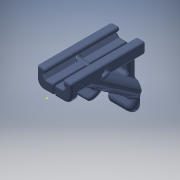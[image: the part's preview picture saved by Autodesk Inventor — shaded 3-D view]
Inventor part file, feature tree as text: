
AUTODESK INVENTOR PART (.ipt)
format: ipt  version: 2016 (Build 200138000, 138)  size: 5,970,432 bytes
history: native  units: mm
features: sketch x29, extrude x28, projected_geometry x27, fillet x26, plane x9, chamfer x3, other x2
ambient origin geometry x8: Origin, YZ Plane, XZ Plane, XY Plane, X Axis, Y Axis, Z Axis, Center Point
bodies: Solid1 (feature_tree)
feature tree (124):
  extrude  "Extrusion1"  Depth=35.0mm
  extrude  "Extrusion2"  Depth=10.0mm
  extrude  "Extrusion3"  Depth=12.0mm
  other  "Work Axis2"
  other  "Work Point2"
  plane  "Work Plane2"
  extrude  "Extrusion5"  Depth=12.0mm
  sketch  "Sketch9"  dims[d14=15.0mm d15=10.0mm d16=15.0mm d17=0.0mm]
  extrude  "Extrusion4"  TaperAngle=90.0deg  [1 undecoded]
  plane  "Work Plane3"
  sketch  "Sketch10"  dims[d18=17.0mm d19=10.0mm d20=130.0mm d21=0.0mm d23=35.531179mm d24=18.5mm d25=18.5mm d26=7.5mm]
  plane  "Work Plane5"
  extrude  "Extrusion8"  Depth=10.0mm
  fillet  "Fillet3"  Radius=15.0mm
  extrude  "Extrusion9"  Depth=10.0mm
  fillet  "Fillet5"  Radius=130.0mm
  fillet  "Fillet6"  Radius=35.531179mm
  fillet  "Fillet7"  Radius=18.5mm
  fillet  "Fillet8"  Radius=18.5mm
  fillet  "Fillet9"  Radius=7.5mm
  extrude  "Extrusion10"  Depth=36.0mm TaperAngle=0.0deg
  fillet  "Fillet10"  Radius=35.75mm
  fillet  "Fillet11"  [1 undecoded]
  fillet  "Fillet12"  Radius=34.0mm
  plane  "Work Plane4"
  extrude  "Extrusion11"  Depth=5.0mm
  extrude  "Extrusion12"  Depth=13.5mm TaperAngle=0.0deg
  extrude  "Extrusion13"  Depth=5.0mm
  fillet  "Fillet13"  Radius=2.0mm
  fillet  "Fillet14"  Radius=2.0mm
  fillet  "Fillet15"  Radius=2.0mm
  sketch  "Sketch22"  dims[d115=3.0mm d116=3.0mm d117=45.0deg]
  extrude  "Extrusion14"  Depth=9.0mm
  extrude  "Extrusion15"  Depth=8.5mm
  extrude  "Extrusion16"  Depth=3.0mm
  fillet  "Fillet16"  [1 undecoded]
  extrude  "Extrusion17"  Depth=2.0mm
  extrude  "Extrusion18"  Depth=1.0mm
  plane  "Work Plane6"
  extrude  "Extrusion19"  Depth=2.0mm
  sketch  "Sketch27"  dims[d132=5.0mm d133=2.0mm d134=8.0mm d135=8.0mm d136=5.0mm d137=0.0mm]
  extrude  "Extrusion21"  Depth=5.0mm
  extrude  "Extrusion22"  Depth=2.0mm
  fillet  "Fillet17"  Radius=8.0mm
  fillet  "Fillet18"  Radius=8.0mm
  fillet  "Fillet19"  Radius=5.0mm
  extrude  "Extrusion23"  Depth=5.0mm TaperAngle=0.0deg
  extrude  "Extrusion24"  Depth=0.5mm
  fillet  "Fillet20"  Radius=0.5mm
  chamfer  "Chamfer3"  Distance=55.0mm
  chamfer  "Chamfer4"  Distance=15.0mm
  fillet  "Fillet22"  Radius=1.0mm
  extrude  "Extrusion25"  Depth=5.0mm
  plane  "Work Plane7"
  extrude  "Extrusion26"  Depth=2.5mm
  fillet  "Fillet23"  Radius=1.0mm
  plane  "Work Plane8"
  plane  "Work Plane9"
  extrude  "Extrusion27"  Depth=1.0mm
  fillet  "Fillet25"  Radius=1.0mm
  fillet  "Fillet26"  Radius=1.0mm
  fillet  "Fillet28"  Radius=1.0mm
  fillet  "Fillet29"  Radius=1.0mm
  plane  "Work Plane10"
  extrude  "Extrusion28"  Depth=1.0mm
  extrude  "Extrusion29"  Depth=1.0mm
  extrude  "Extrusion30"  Depth=1.0mm
  fillet  "Fillet30"  Radius=1.0mm
  fillet  "Fillet31"  Radius=1.0mm
  fillet  "Fillet32"  Radius=1.0mm
  extrude  "Extrusion31"  Depth=1.0mm
  chamfer  "Chamfer5"  Distance=1.0mm
  sketch  "Sketch1"  dims[d0=135.0mm d1=35.0mm]
  sketch  "Sketch2"  dims[d2=10.0mm d3=0.0mm d4=10.0mm]
  projected_geometry  "Projected Loop1"
  sketch  "Sketch3"  dims[d5=15.0mm d6=0.0mm d7=12.0mm]
  projected_geometry  "Projected Loop2"
  sketch  "Sketch4"  dims[d10=9.599311mm d11=12.0mm]
  projected_geometry  "Projected Loop3"
  sketch  "Sketch5"  dims[d12=35.0mm d13=90.0deg]
  sketch  "Sketch12"  dims[d27=7.5mm d28=36.0mm d29=0.0mm d30=35.75mm d31=0.0mm d32=-5.0mm d44=34.0mm d45=0.0mm]
  projected_geometry  "Projected Loop11"
  sketch  "Sketch14"  dims[d46=5.0mm d48=5.0mm]
  sketch  "Sketch18"  dims[d49=5.0mm d50=13.5mm d51=0.0mm]
  projected_geometry  "Projected Loop26"
  sketch  "Sketch19"  dims[d60=5.0mm d61=5.0mm d62=2.0mm d63=2.0mm d64=2.0mm]
  sketch  "Sketch20"  dims[d67=2.0mm d112=9.0mm]
  sketch  "Sketch21"  dims[d113=8.5mm d114=8.5mm]
  sketch  "Sketch23"  dims[d118=13.5mm d119=0.0mm d120=2.0mm]
  projected_geometry  "Projected Loop28"
  sketch  "Sketch24"  dims[d121=2.0mm d122=1.0mm]
  projected_geometry  "Projected Loop29"
  projected_geometry  "Projected Loop30"
  projected_geometry  "Projected Loop31"
  sketch  "Sketch25"  dims[d123=-17.5mm d125=2.0mm]
  sketch  "Sketch26"  dims[d128=13.5mm d129=0.0mm d131=5.0mm]
  projected_geometry  "Projected Loop32"
  projected_geometry  "Projected Loop33"
  projected_geometry  "Projected Loop34"
  projected_geometry  "Projected Loop35"
  sketch  "Sketch28"  dims[d138=4.25mm d139=5.0mm d140=0.0mm]
  projected_geometry  "Projected Loop36"
  sketch  "Sketch29"  dims[d141=0.5mm d142=0.5mm d143=0.5mm]
  sketch  "Sketch30"  dims[d144=25.0mm]
  sketch  "Sketch32"  dims[d145=1.0mm]
  projected_geometry  "Projected Loop37"
  sketch  "Sketch33"  dims[d146=1.0mm d147=55.0mm d148=0.0mm]
  projected_geometry  "Projected Loop38"
  projected_geometry  "Projected Loop39"
  sketch  "Sketch35"  dims[d149=4.0mm]
  sketch  "Sketch36"  dims[d150=4.0mm d151=15.0mm d152=0.0mm d153=1.0mm]
  sketch  "Sketch38"  dims[d154=5.0mm d155=5.0mm]
  sketch  "Sketch39"  dims[d156=5.0mm d157=0.0mm d158=2.5mm d160=1.0mm]
  projected_geometry  "Projected Loop50"
  sketch  "Sketch40"  dims[d161=1.5mm d163=1.0mm d164=1.0mm d165=1.5mm d166=1.0mm d167=1.0mm d168=1.5mm d169=1.0mm d170=1.0mm d171=1.5mm d172=1.0mm d173=1.0mm d174=1.5mm d175=1.0mm d176=1.0mm d177=1.5mm d178=1.0mm d179=1.0mm d180=1.5mm d181=1.0mm d182=1.0mm d183=1.5mm d184=1.0mm d185=1.0mm d186=1.5mm d187=1.0mm d188=1.0mm d189=1.5mm d190=1.0mm d191=1.0mm d192=1.5mm d193=1.0mm d194=1.0mm d195=1.5mm d196=1.0mm d197=1.0mm d198=1.5mm d199=1.0mm d200=1.0mm d201=1.5mm d202=1.0mm d203=1.0mm d204=1.5mm d205=1.0mm d206=1.0mm d207=1.5mm d208=1.0mm d209=1.0mm d210=1.5mm d211=1.0mm d212=6.5mm d213=0.0mm d214=1.5mm d215=50.75mm d216=0.0mm d217=1.0mm d218=1.5mm d219=1.0mm d220=90.0deg d221=1.5mm d222=1.0mm d223=1.5mm d224=1.0mm d225=1.0mm d226=1.0mm d227=1.5mm d228=1.0mm d229=1.5mm d230=1.0mm d231=1.0mm d232=1.0mm d233=1.5mm d234=1.0mm d235=1.5mm d236=1.0mm d237=1.0mm d238=1.0mm d239=1.5mm d240=1.0mm d241=1.5mm d242=1.0mm d243=1.0mm d244=1.0mm d245=1.5mm d246=1.0mm d247=1.5mm d248=1.0mm d249=1.0mm d250=1.0mm d251=1.5mm d252=1.0mm d253=1.5mm d254=1.0mm d255=1.0mm d256=1.0mm d257=1.5mm d258=1.0mm d259=1.5mm d260=1.0mm d261=1.0mm d262=1.0mm d263=1.5mm d264=1.0mm d265=1.5mm d266=1.0mm d267=1.0mm d268=1.0mm d269=1.5mm d270=1.0mm d271=1.5mm d272=1.0mm d273=1.0mm d274=1.0mm d275=1.5mm d276=1.0mm d277=1.5mm d278=1.0mm d279=1.0mm d280=1.0mm d281=1.5mm d282=1.0mm d283=1.5mm d284=1.0mm d285=7.5mm d286=0.0mm d287=1.5mm d290=3.75mm d291=0.0mm d292=25.5mm d293=0.0mm d294=25.5mm d295=0.0mm d296=4.25mm d297=0.5mm d298=2.25mm d299=0.0mm d300=0.5mm d301=0.5mm d302=4.25mm d303=0.0mm d304=5.0mm d305=0.0mm d306=0.5mm d307=0.0mm d308=0.2mm d309=2.0mm d310=45.0deg d311=0.2mm d312=2.0mm d313=45.0deg d315=1.5mm d316=1.5mm d317=1.5mm d321=49.0mm d322=0.0mm d323=12.0mm d324=48.0mm d325=-14.0mm d326=8.0mm d327=9.5mm d328=16.75mm d329=0.0mm d330=0.0mm d331=2.75mm d333=-55.0mm d334=-42.0mm d335=38.5mm d336=0.0mm d337=2.0mm d338=1.0mm d341=2.0mm d342=2.0mm d343=-76.2mm d344=67.75mm d345=0.0mm d346=48.0mm d347=5.0mm d348=0.0mm d350=90.0deg d351=10.0mm d352=35.0mm d353=8.0mm d354=0.0mm d355=2.25mm d356=1.5mm d357=7.0mm d358=2.0mm d359=16.75mm d360=0.0mm d361=0.5mm d362=2.0mm d363=45.0deg]
  projected_geometry  "Projected Loop51"
  projected_geometry  "Projected Loop52"
  projected_geometry  "Project Cut Edges1"
  projected_geometry  "Project Cut Edges2"
  projected_geometry  "Project Cut Edges3"
  projected_geometry  "Project Cut Edges4"
  projected_geometry  "Project Cut Edges5"
  projected_geometry  "Project Cut Edges6"
  projected_geometry  "Project Cut Edges8"
note: 3 required parameter values undecoded (feature->parameter linkage not recoverable at this tier; creation-order binding heuristic only, values carry confidence <= 0.55)
